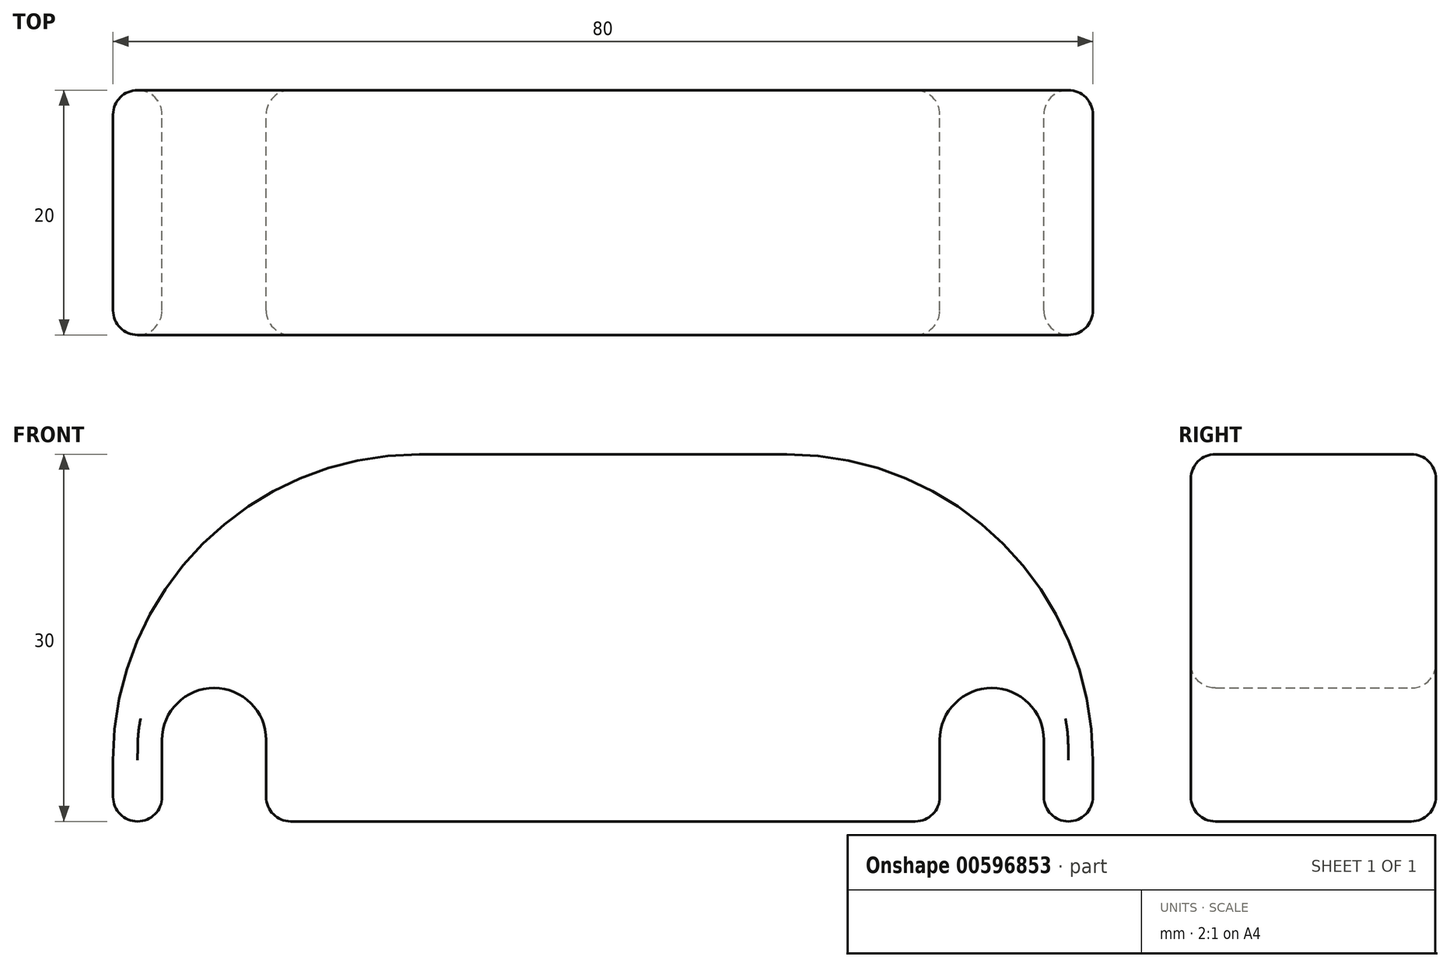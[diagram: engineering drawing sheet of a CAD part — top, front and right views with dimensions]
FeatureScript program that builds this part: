
annotation { "Feature Type Name" : "Feature", "Feature Type Description" : "" }
export const myFeature = defineFeature(function(context is Context, id is Id, definition is map)
    precondition{}
    {
        {
            var Q0;
            Q0=qCreatedBy(makeId("Front.planeOp"),FACE);
            var sketch = newSketch(context, id + "F0", { "sketchPlane" : qUnion([Q0])});
            skLineSegment(sketch, "E0.bottom", {"start": v(-15, 15) * mm, "end": v(15, 15) * mm});
            skLineSegment(sketch, "E0.top", {"start": v(-40, -15) * mm, "end": v(-36, -15) * mm});
            skLineSegment(sketch, "E0.left", {"start": v(-40, -10) * mm, "end": v(-40, -15) * mm});
            skLineSegment(sketch, "E0.right", {"start": v(40, -10) * mm, "end": v(40, -15) * mm});
            skPoint(sketch, "E0.middle", {"position": v(0, 0) * mm});
            skPoint(sketch, "E1.visualSharp", {"position": v(-40, 15) * mm});
            skArc(sketch, "E1.filletArc", {"start": v(-15, 15) * mm, "mid": v(-32.68, 7.68) * mm, "end": v(-40, -10) * mm});
            skPoint(sketch, "E2.visualSharp", {"position": v(40, 15) * mm});
            skArc(sketch, "E2.filletArc", {"start": v(40, -10) * mm, "mid": v(32.68, 7.68) * mm, "end": v(15, 15) * mm});
            skLineSegment(sketch, "E3.bottom", {"start": v(-36, -7) * mm, "end": v(36, -7) * mm, "construction": true});
            skLineSegment(sketch, "E3.top", {"start": v(-36, -23) * mm, "end": v(36, -23) * mm, "construction": true});
            skLineSegment(sketch, "E3.left", {"start": v(-36, -7) * mm, "end": v(-36, -23) * mm, "construction": true});
            skLineSegment(sketch, "E3.right", {"start": v(36, -7) * mm, "end": v(36, -23) * mm, "construction": true});
            skPoint(sketch, "E3.middle", {"position": v(0, -15) * mm});
            skArc(sketch, "E4", {"start": v(-27.5, -8.36) * mm, "mid": v(-31.75, -4.1) * mm, "end": v(-36, -8.36) * mm});
            skArc(sketch, "E5", {"start": v(36, -8.36) * mm, "mid": v(31.75, -4.1) * mm, "end": v(27.5, -8.36) * mm});
            skLineSegment(sketch, "E6", {"start": v(-27.5, -8.36) * mm, "end": v(-27.5, -15) * mm});
            skLineSegment(sketch, "E7", {"start": v(-36, -15) * mm, "end": v(-36, -8.36) * mm});
            skLineSegment(sketch, "E8", {"start": v(27.5, -8.36) * mm, "end": v(27.5, -15) * mm});
            skLineSegment(sketch, "E9", {"start": v(36, -15) * mm, "end": v(36, -8.36) * mm});
            skLineSegment(sketch, "E10.trimOffspring", {"start": v(36, -15) * mm, "end": v(40, -15) * mm});
            skLineSegment(sketch, "E11.trimOffspring", {"start": v(-27.5, -15) * mm, "end": v(27.5, -15) * mm});
            skSolve(sketch);
        }
        {
            var Q0;
            Q0=makeQuery(id+"F0.imprint","IMPRINT",FACE,{"disambiguationData":[TD([[makeQuery(id+"F0.imprint","IMPRINT",EDGE,{"derivedFrom":sQuery(id+"F0.wireOp",EDGE,"E0.bottom")}),-1.0]])]});
            extrude(context, id + "F1", {"entities" : qUnion([Q0]), "depth" : 20 * mm, "offsetDistance" : 25 * mm});
        }
        {
            var Q0;
            Q0=makeQuery(id+"F1.opExtrude","SWEPT_EDGE",EDGE,{"disambiguationData":[OSD([sQuery(id+"F0.wireOp",EDGE,"E9"),sQuery(id+"F0.wireOp",EDGE,"E10.trimOffspring")])]});
            var Q1;
            Q1=makeQuery(id+"F1.opExtrude","SWEPT_EDGE",EDGE,{"disambiguationData":[OSD([sQuery(id+"F0.wireOp",EDGE,"E8"),sQuery(id+"F0.wireOp",EDGE,"E11.trimOffspring")])]});
            var Q2;
            Q2=makeQuery(id+"F1.opExtrude","SWEPT_EDGE",EDGE,{"disambiguationData":[OSD([sQuery(id+"F0.wireOp",EDGE,"E0.right"),sQuery(id+"F0.wireOp",EDGE,"E10.trimOffspring")])]});
            var Q3;
            Q3=makeQuery(id+"F1.opExtrude","SWEPT_EDGE",EDGE,{"disambiguationData":[OSD([sQuery(id+"F0.wireOp",EDGE,"E6"),sQuery(id+"F0.wireOp",EDGE,"E11.trimOffspring")])]});
            var Q4;
            Q4=makeQuery(id+"F1.opExtrude","SWEPT_EDGE",EDGE,{"disambiguationData":[OSD([sQuery(id+"F0.wireOp",EDGE,"E0.top"),sQuery(id+"F0.wireOp",EDGE,"E7")])]});
            var Q5;
            Q5=makeQuery(id+"F1.opExtrude","SWEPT_EDGE",EDGE,{"disambiguationData":[OSD([sQuery(id+"F0.wireOp",EDGE,"E0.top"),sQuery(id+"F0.wireOp",EDGE,"E0.left")])]});
            fillet(context, id + "F2", {"entities" : qUnion([Q0, Q1, Q2, Q3, Q4, Q5]), "radius" : 2 * mm, "tangentPropagation" : true, "allowEdgeOverflow" : false});
        }
        {
            var Q0;
            Q0=makeQuery(id+"F1.opExtrude","CAP_EDGE",EDGE,{"disambiguationData":[OSD([sQuery(id+"F0.wireOp",EDGE,"E0.bottom")])],"isStart":true});
            var Q1;
            Q1=makeQuery(id+"F1.opExtrude","CAP_EDGE",EDGE,{"disambiguationData":[OSD([sQuery(id+"F0.wireOp",EDGE,"E2.filletArc")])],"isStart":false});
            fillet(context, id + "F3", {"entities" : qUnion([Q0, Q1]), "radius" : 2 * mm, "tangentPropagation" : true, "allowEdgeOverflow" : false});
        }
    });
